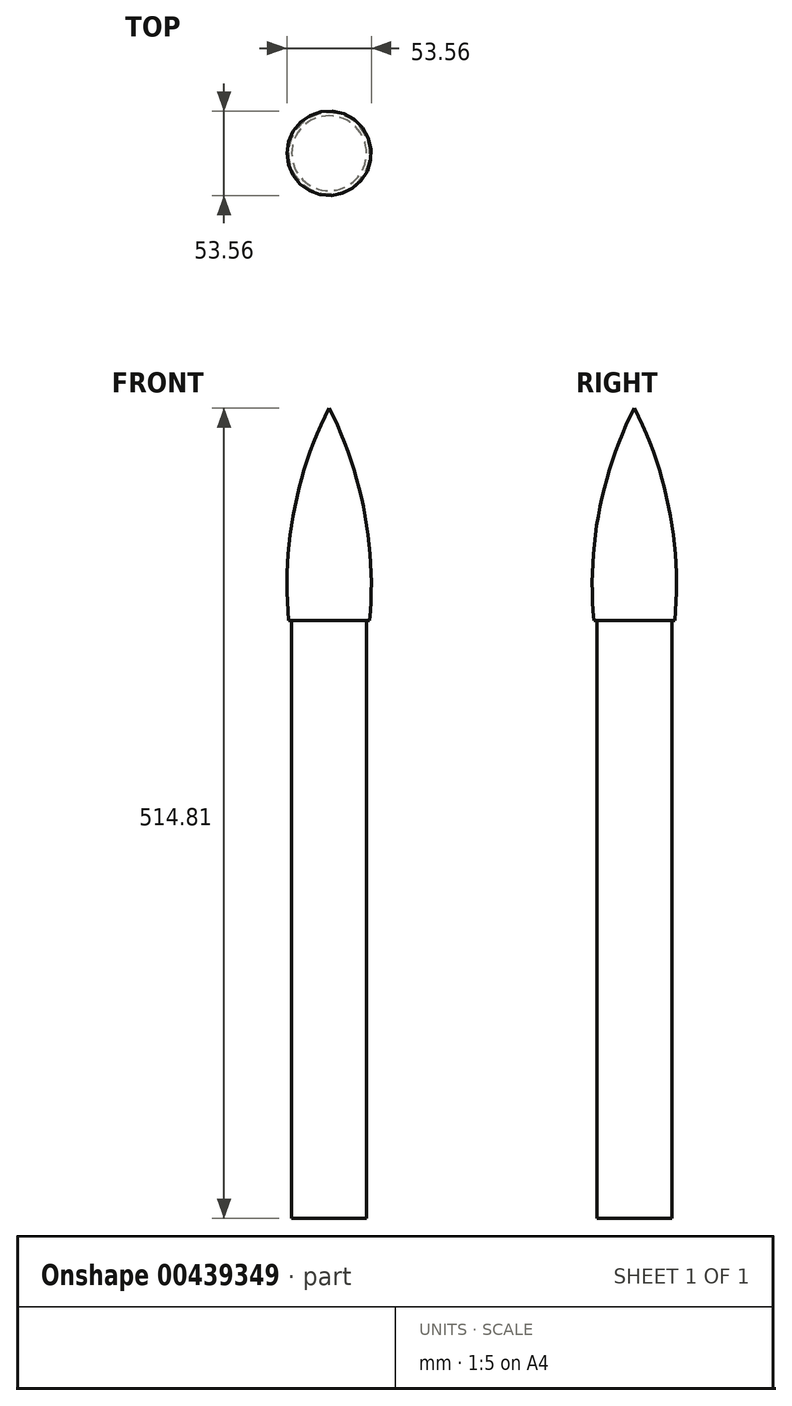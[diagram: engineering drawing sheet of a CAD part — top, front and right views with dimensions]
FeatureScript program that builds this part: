
annotation { "Feature Type Name" : "Feature", "Feature Type Description" : "" }
export const myFeature = defineFeature(function(context is Context, id is Id, definition is map)
    precondition{}
    {
        {
            var Q0;
            Q0=qCreatedBy(makeId("Front.planeOp"),FACE);
            var sketch = newSketch(context, id + "F0", { "sketchPlane" : qUnion([Q0])});
            skLineSegment(sketch, "E0", {"start": v(0, 0) * mm, "end": v(25.75, 0) * mm});
            skLineSegment(sketch, "E1", {"start": v(0, -15) * mm, "end": v(23.75, -15) * mm});
            skLineSegment(sketch, "E2", {"start": v(0, 135) * mm, "end": v(0, -15) * mm});
            skLineSegment(sketch, "E3", {"start": v(23.75, -15) * mm, "end": v(23.75, 0) * mm});
            skArc(sketch, "E4", {"start": v(25.75, 0) * mm, "mid": v(22.37, 69.31) * mm, "end": v(0, 135) * mm});
            skSolve(sketch);
        }
        {
            var Q0;
            {var subQ4=sQuery(id+"F0.wireOp",EDGE,"E4");Q0=makeQuery(id+"F0.imprint","IMPRINT",FACE,{"disambiguationData":[TD([[makeQuery(id+"F0.imprint","IMPRINT",EDGE,{"derivedFrom":subQ4}),1.0]])]});}
            var Q1;
            {var subQ4=sQuery(id+"F0.wireOp",EDGE,"E1");Q1=makeQuery(id+"F0.imprint","IMPRINT",FACE,{"disambiguationData":[TD([[makeQuery(id+"F0.imprint","IMPRINT",EDGE,{"derivedFrom":subQ4}),1.0]])]});}
            var Q2;
            Q2=sQuery(id+"F0.wireOp",EDGE,"E2");
            revolve(context, id + "F1", {"entities" : qUnion([Q0, Q1]), "axis" : qUnion([Q2]), "revolveType" : RevolveType.FULL});
        }
        {
            var Q0;
            Q0=makeQuery(id+"F1.opRevolve","SWEPT_FACE",FACE,{"disambiguationData":[OSD([sQuery(id+"F0.wireOp",EDGE,"E1")])]});
            extrude(context, id + "F2", {"entities" : qUnion([Q0]), "operationType" : NewBodyOperationType.ADD, "depth" : 364.8 * mm});
        }
    });
